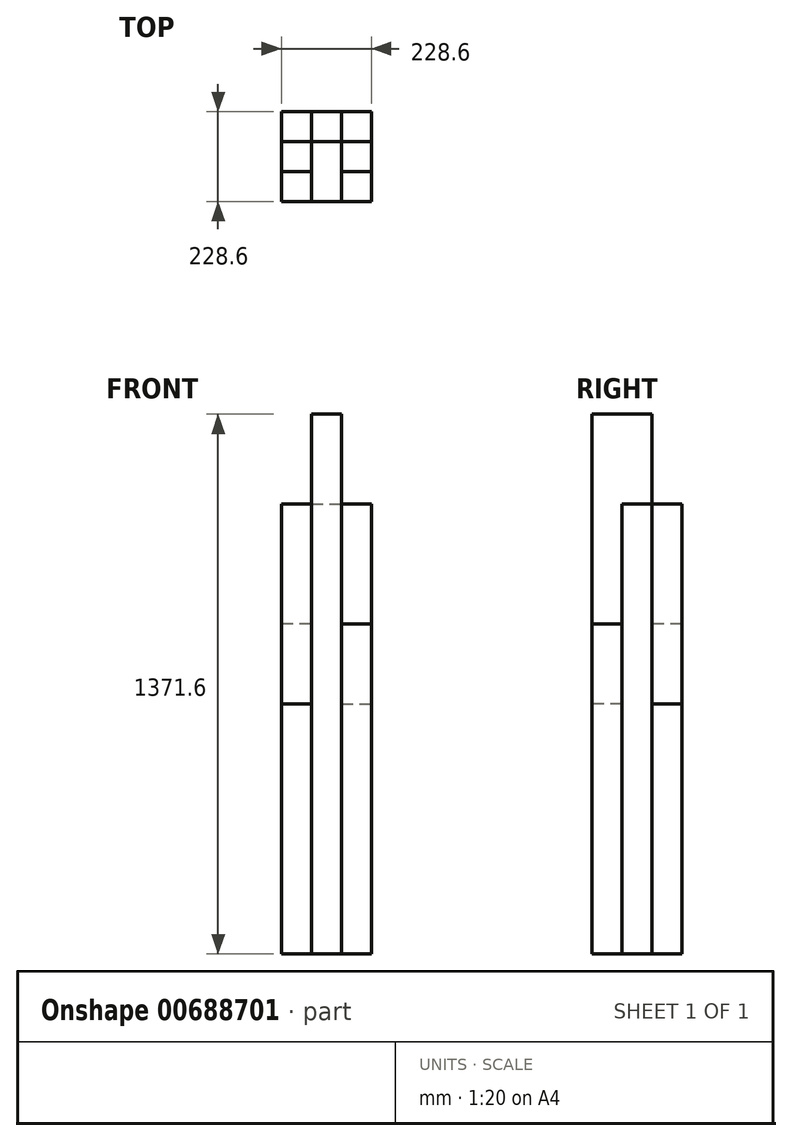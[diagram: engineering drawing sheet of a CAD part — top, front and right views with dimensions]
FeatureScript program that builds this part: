
annotation { "Feature Type Name" : "Feature", "Feature Type Description" : "" }
export const myFeature = defineFeature(function(context is Context, id is Id, definition is map)
    precondition{}
    {
        {
            var Q0;
            Q0=qCreatedBy(makeId("Top.planeOp"),FACE);
            var sketch = newSketch(context, id + "F0", { "sketchPlane" : qUnion([Q0])});
            skLineSegment(sketch, "E0.bottom", {"start": v(38.1, 114.3) * mm, "end": v(114.3, 114.3) * mm});
            skLineSegment(sketch, "E0.top", {"start": v(-114.3, -114.3) * mm, "end": v(-38.1, -114.3) * mm});
            skLineSegment(sketch, "E0.left", {"start": v(-114.3, -38.1) * mm, "end": v(-114.3, -114.3) * mm});
            skLineSegment(sketch, "E0.right", {"start": v(114.3, 114.3) * mm, "end": v(114.3, 38.1) * mm});
            skPoint(sketch, "E0.middle", {"position": v(0, 0) * mm});
            skLineSegment(sketch, "E1", {"start": v(-38.1, -114.3) * mm, "end": v(-38.1, -38.1) * mm});
            skLineSegment(sketch, "E2", {"start": v(-38.1, -38.1) * mm, "end": v(-114.3, -38.1) * mm});
            skLineSegment(sketch, "E3", {"start": v(114.3, 114.3) * mm, "end": v(38.1, 114.3) * mm});
            skLineSegment(sketch, "E4", {"start": v(38.1, 114.3) * mm, "end": v(38.1, 38.1) * mm});
            skLineSegment(sketch, "E5", {"start": v(38.1, 38.1) * mm, "end": v(114.3, 38.1) * mm});
            skPoint(sketch, "E6.orphan", {"position": v(-114.3, 114.3) * mm});
            skPoint(sketch, "E7.orphan", {"position": v(114.3, -114.3) * mm});
            skSolve(sketch);
        }
        {
            var Q0;
            Q0 = qSketchRegion(id + "F0", true);
            extrude(context, id + "F1", {"entities" : qUnion([Q0]), "depth" : 635 * mm, "offsetDistance" : 25.4 * mm});
        }
        {
            var Q0;
            Q0=qCreatedBy(makeId("Top.planeOp"),FACE);
            var sketch = newSketch(context, id + "F2", { "sketchPlane" : qUnion([Q0])});
            skLineSegment(sketch, "E8.bottom", {"start": v(-38.1, 114.3) * mm, "end": v(-114.3, 114.3) * mm});
            skLineSegment(sketch, "E8.top", {"start": v(114.3, -114.3) * mm, "end": v(38.1, -114.3) * mm});
            skLineSegment(sketch, "E8.left", {"start": v(114.3, -38.1) * mm, "end": v(114.3, -114.3) * mm});
            skLineSegment(sketch, "E8.right", {"start": v(-114.3, 114.3) * mm, "end": v(-114.3, 38.1) * mm});
            skPoint(sketch, "E8.middle", {"position": v(0, 0) * mm});
            skLineSegment(sketch, "E9", {"start": v(-114.3, 114.3) * mm, "end": v(-38.1, 114.3) * mm});
            skLineSegment(sketch, "E10", {"start": v(-38.1, 114.3) * mm, "end": v(-38.1, 38.1) * mm});
            skLineSegment(sketch, "E11", {"start": v(-38.1, 38.1) * mm, "end": v(-114.3, 38.1) * mm});
            skLineSegment(sketch, "E12", {"start": v(114.3, -114.3) * mm, "end": v(114.3, -38.1) * mm});
            skLineSegment(sketch, "E13", {"start": v(114.3, -38.1) * mm, "end": v(38.1, -38.1) * mm});
            skLineSegment(sketch, "E14", {"start": v(38.1, -38.1) * mm, "end": v(38.1, -114.3) * mm});
            skPoint(sketch, "E15.orphan", {"position": v(-114.3, -114.3) * mm});
            skPoint(sketch, "E16.orphan", {"position": v(114.3, 114.3) * mm});
            skSolve(sketch);
        }
        {
            var Q0;
            Q0 = qSketchRegion(id + "F2", true);
            extrude(context, id + "F3", {"entities" : qUnion([Q0]), "depth" : 838.2 * mm, "offsetDistance" : 25.4 * mm});
        }
        {
            var Q0;
            Q0=qCreatedBy(makeId("Top.planeOp"),FACE);
            var sketch = newSketch(context, id + "F4", { "sketchPlane" : qUnion([Q0])});
            skLineSegment(sketch, "E17.bottom", {"start": v(-38.1, 114.3) * mm, "end": v(38.1, 114.3) * mm});
            skLineSegment(sketch, "E17.left", {"start": v(-114.3, 38.1) * mm, "end": v(-114.3, -38.1) * mm});
            skLineSegment(sketch, "E17.right", {"start": v(114.3, 38.1) * mm, "end": v(114.3, -38.1) * mm});
            skPoint(sketch, "E17.middle", {"position": v(0, 0) * mm});
            skLineSegment(sketch, "E18", {"start": v(-114.3, -38.1) * mm, "end": v(-38.1, -38.1) * mm});
            skLineSegment(sketch, "E19", {"start": v(114.3, -38.1) * mm, "end": v(114.3, 38.1) * mm});
            skLineSegment(sketch, "E20", {"start": v(114.3, 38.1) * mm, "end": v(38.1, 38.1) * mm});
            skLineSegment(sketch, "E21", {"start": v(38.1, 38.1) * mm, "end": v(38.1, 114.3) * mm});
            skLineSegment(sketch, "E22", {"start": v(38.1, 114.3) * mm, "end": v(-38.1, 114.3) * mm});
            skLineSegment(sketch, "E23", {"start": v(-38.1, 114.3) * mm, "end": v(-38.1, 38.1) * mm});
            skLineSegment(sketch, "E24", {"start": v(-38.1, 38.1) * mm, "end": v(-114.3, 38.1) * mm});
            skLineSegment(sketch, "E25", {"start": v(-38.1, 38.1) * mm, "end": v(-38.1, -38.1) * mm});
            skLineSegment(sketch, "E26", {"start": v(38.1, 38.1) * mm, "end": v(38.1, -38.1) * mm});
            skLineSegment(sketch, "E27", {"start": v(-38.1, 38.1) * mm, "end": v(38.1, 38.1) * mm});
            skLineSegment(sketch, "E28.trimOffspring", {"start": v(38.1, -38.1) * mm, "end": v(114.3, -38.1) * mm});
            skPoint(sketch, "E29.orphan", {"position": v(-114.3, -114.3) * mm});
            skPoint(sketch, "E30.orphan", {"position": v(-114.3, 114.3) * mm});
            skPoint(sketch, "E31.orphan", {"position": v(114.3, 114.3) * mm});
            skPoint(sketch, "E32.orphan", {"position": v(114.3, -114.3) * mm});
            skSolve(sketch);
        }
        {
            var Q0;
            Q0 = qSketchRegion(id + "F4", true);
            extrude(context, id + "F5", {"entities" : qUnion([Q0]), "depth" : 1143 * mm, "offsetDistance" : 25.4 * mm});
        }
        {
            var Q0;
            Q0=qCreatedBy(makeId("Top.planeOp"),FACE);
            var sketch = newSketch(context, id + "F6", { "sketchPlane" : qUnion([Q0])});
            skLineSegment(sketch, "E33.top", {"start": v(-114.3, -114.3) * mm, "end": v(114.3, -114.3) * mm});
            skPoint(sketch, "E33.middle", {"position": v(0, 0) * mm});
            skLineSegment(sketch, "E34", {"start": v(-38.1, -114.3) * mm, "end": v(-38.1, 38.1) * mm});
            skLineSegment(sketch, "E35", {"start": v(-38.1, 38.1) * mm, "end": v(38.1, 38.1) * mm});
            skLineSegment(sketch, "E36", {"start": v(38.1, 38.1) * mm, "end": v(38.1, -114.3) * mm});
            skLineSegment(sketch, "E37", {"start": v(-38.1, -38.1) * mm, "end": v(38.1, -38.1) * mm});
            skPoint(sketch, "E33.bottom.start.orphan", {"position": v(-114.3, 114.3) * mm});
            skPoint(sketch, "E33.right.start.orphan", {"position": v(114.3, 114.3) * mm});
            skSolve(sketch);
        }
        {
            var Q0;
            Q0 = qSketchRegion(id + "F6", true);
            extrude(context, id + "F7", {"entities" : qUnion([Q0]), "depth" : 1371.6 * mm, "offsetDistance" : 25.4 * mm});
        }
    });
